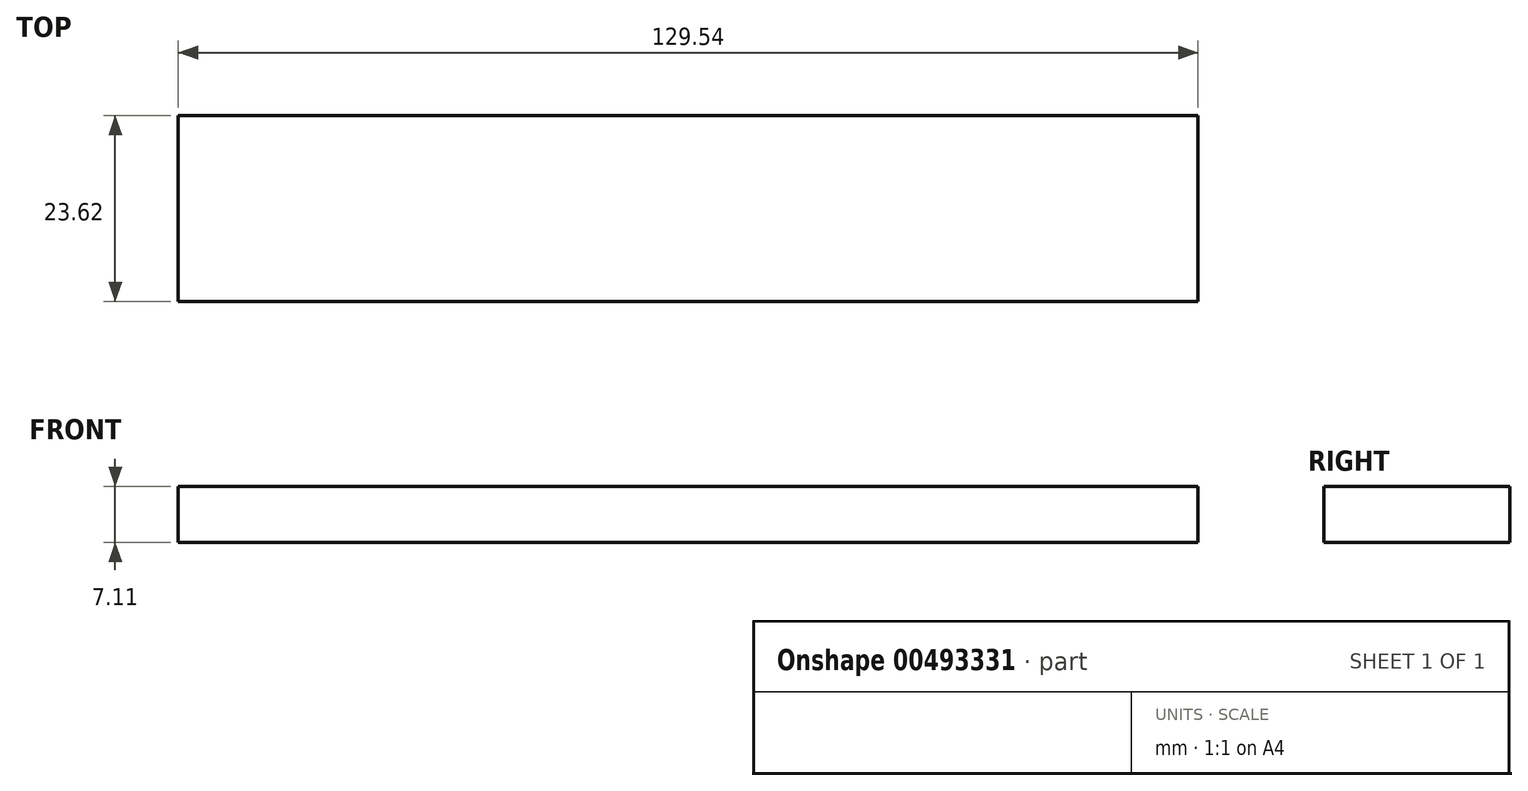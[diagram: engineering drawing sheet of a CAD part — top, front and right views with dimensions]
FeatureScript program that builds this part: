
annotation { "Feature Type Name" : "Feature", "Feature Type Description" : "" }
export const myFeature = defineFeature(function(context is Context, id is Id, definition is map)
    precondition{}
    {
        {
            var Q0;
            Q0=qCreatedBy(makeId("Top.planeOp"),FACE);
            var sketch = newSketch(context, id + "F0", { "sketchPlane" : qUnion([Q0])});
            skLineSegment(sketch, "E0.bottom", {"start": v(-67.04, 42.13) * mm, "end": v(62.5, 42.13) * mm});
            skLineSegment(sketch, "E0.top", {"start": v(-67.04, 18.5) * mm, "end": v(62.5, 18.5) * mm});
            skLineSegment(sketch, "E0.left", {"start": v(-67.04, 42.13) * mm, "end": v(-67.04, 18.5) * mm});
            skLineSegment(sketch, "E0.right", {"start": v(62.5, 42.13) * mm, "end": v(62.5, 18.5) * mm});
            skSolve(sketch);
        }
        {
            var Q0;
            Q0=makeQuery(id+"F0.imprint","IMPRINT",FACE,{"disambiguationData":[TD([[makeQuery(id+"F0.imprint","IMPRINT",EDGE,{"derivedFrom":sQuery(id+"F0.wireOp",EDGE,"E0.bottom")}),-1.0]])]});
            extrude(context, id + "F1", {"entities" : qUnion([Q0]), "depth" : 7.11 * mm});
        }
    });
